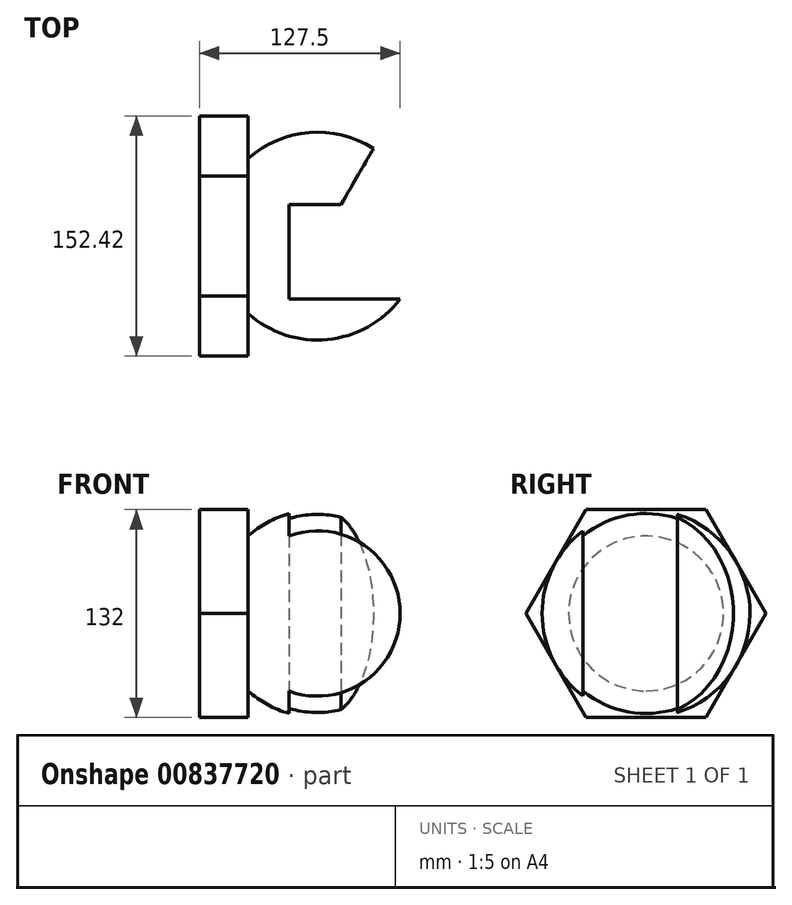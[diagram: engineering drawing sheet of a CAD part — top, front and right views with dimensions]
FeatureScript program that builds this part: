
annotation { "Feature Type Name" : "Feature", "Feature Type Description" : "" }
export const myFeature = defineFeature(function(context is Context, id is Id, definition is map)
    precondition{}
    {
        {
            var Q0;
            Q0=qCreatedBy(makeId("Right.planeOp"),FACE);
            var sketch = newSketch(context, id + "F0", { "sketchPlane" : qUnion([Q0])});
            skCircle(sketch, "E0.cCircle", {"center": v(0, 0) * mm, "radius": 66 * mm, "construction": true});
            skLineSegment(sketch, "E0.0", {"start": v(-38.1, 66) * mm, "end": v(38.1, 66) * mm});
            skLineSegment(sketch, "E0.1", {"start": v(38.1, 66) * mm, "end": v(76.21, 0) * mm});
            skLineSegment(sketch, "E0.2", {"start": v(76.21, 0) * mm, "end": v(38.1, -66) * mm});
            skLineSegment(sketch, "E0.3", {"start": v(38.1, -66) * mm, "end": v(-38.1, -66) * mm});
            skLineSegment(sketch, "E0.4", {"start": v(-38.1, -66) * mm, "end": v(-76.21, 0) * mm});
            skLineSegment(sketch, "E0.5", {"start": v(-76.21, 0) * mm, "end": v(-38.1, 66) * mm});
            skPoint(sketch, "E0.0.midPoint", {"position": v(0, 66) * mm});
            skSolve(sketch);
        }
        {
            var Q0;
            Q0=makeQuery(id+"F0.imprint","IMPRINT",FACE,{"disambiguationData":[TD([[makeQuery(id+"F0.imprint","IMPRINT",EDGE,{"derivedFrom":sQuery(id+"F0.wireOp",EDGE,"E0.0")}),-1.0]])]});
            extrude(context, id + "F1", {"entities" : qUnion([Q0]), "depth" : 31 * mm, "offsetDistance" : 25 * mm});
        }
        {
            var Q0;
            Q0=qCreatedBy(makeId("Front.planeOp"),FACE);
            var sketch = newSketch(context, id + "F2", { "sketchPlane" : qUnion([Q0])});
            skArc(sketch, "E1", {"start": v(141, 0) * mm, "mid": v(75, 66) * mm, "end": v(9, 0) * mm});
            skLineSegment(sketch, "E2.0.0", {"start": v(0, 66) * mm, "end": v(0, 0) * mm});
            skLineSegment(sketch, "E2.0.1", {"start": v(0, 0) * mm, "end": v(31, 0) * mm});
            skLineSegment(sketch, "E2.0.2", {"start": v(31, 0) * mm, "end": v(31, 66) * mm});
            skLineSegment(sketch, "E2.0.3", {"start": v(31, 66) * mm, "end": v(0, 66) * mm});
            skLineSegment(sketch, "E3.0.0", {"start": v(0, 0) * mm, "end": v(0, -66) * mm});
            skLineSegment(sketch, "E3.0.1", {"start": v(0, -66) * mm, "end": v(31, -66) * mm});
            skLineSegment(sketch, "E3.0.2", {"start": v(31, -66) * mm, "end": v(31, 0) * mm});
            skLineSegment(sketch, "E3.0.3", {"start": v(31, 0) * mm, "end": v(0, 0) * mm});
            skLineSegment(sketch, "E4", {"start": v(57, 66) * mm, "end": v(57, 63.5) * mm});
            skPoint(sketch, "E5.trimOffspring.end.orphan", {"position": v(57, -66) * mm});
            skLineSegment(sketch, "E6", {"start": v(141, 0) * mm, "end": v(9, 0) * mm});
            skSolve(sketch);
        }
        {
            var Q0;
            {var subQ0=sQuery(id+"F2.wireOp",EDGE,"E6");Q0=makeQuery(id+"F2.imprint","IMPRINT",FACE,{"disambiguationData":[TD([[makeQuery(id+"F2.imprint","IMPRINT",EDGE,{"derivedFrom":subQ0}),-1.0]])]});}
            var Q1;
            Q1=sQuery(id+"F2.wireOp",EDGE,"E6");
            revolve(context, id + "F3", {"operationType" : NewBodyOperationType.ADD, "surfaceOperationType" : NewSurfaceOperationType.NEW, "entities" : qUnion([Q0]), "axis" : qUnion([Q1]), "revolveType" : RevolveType.FULL});
        }
        {
            var Q0;
            Q0=makeQuery(id+"F1.opExtrude","SWEPT_FACE",FACE,{"disambiguationData":[OSD([sQuery(id+"F0.wireOp",EDGE,"E0.3")])]});
            cPlane(context, id + "F4", {"entities" : qUnion([Q0]), "cplaneType" : CPlaneType.OFFSET, "offset" : 0 * mm, "oppositeDirection" : true, "width" : 150 * mm, "height" : 150 * mm});
        }
        {
            var Q0;
            Q0=qCreatedBy(id+"F4.planeOp",FACE);
            var sketch = newSketch(context, id + "F5", { "sketchPlane" : qUnion([Q0])});
            skArc(sketch, "E7", {"start": v(31, -49.2) * mm, "mid": v(141, 0) * mm, "end": v(31, 49.2) * mm});
            skLineSegment(sketch, "E8", {"start": v(75, 40) * mm, "end": v(152.64, 40) * mm});
            skLineSegment(sketch, "E9", {"start": v(152.64, 40) * mm, "end": v(152.64, 0) * mm});
            skLineSegment(sketch, "E10", {"start": v(75, 40) * mm, "end": v(57, 40) * mm});
            skLineSegment(sketch, "E11", {"start": v(57, 40) * mm, "end": v(57, 0) * mm});
            skLineSegment(sketch, "E12", {"start": v(57, 0) * mm, "end": v(57, -20) * mm});
            skLineSegment(sketch, "E13", {"start": v(57, -20) * mm, "end": v(152.64, -20) * mm});
            skLineSegment(sketch, "E14", {"start": v(152.64, -20) * mm, "end": v(152.64, 0) * mm});
            skSolve(sketch);
        }
        {
            var Q0;
            {var subQ4=sQuery(id+"F5.wireOp",EDGE,"E10");Q0=makeQuery(id+"F5.imprint","IMPRINT",FACE,{"disambiguationData":[TD([[makeQuery(id+"F5.imprint","IMPRINT",EDGE,{"derivedFrom":subQ4}),1.0]])]});}
            extrude(context, id + "F6", {"entities" : qUnion([Q0]), "operationType" : NewBodyOperationType.REMOVE, "oppositeDirection" : true, "depth" : 138 * mm, "offsetDistance" : 25 * mm});
        }
        {
            var Q0;
            Q0=makeQuery(id+"F1.opExtrude","SWEPT_FACE",FACE,{"disambiguationData":[OSD([sQuery(id+"F0.wireOp",EDGE,"E0.3")])]});
            cPlane(context, id + "F7", {"entities" : qUnion([Q0]), "cplaneType" : CPlaneType.OFFSET, "offset" : 0 * mm, "width" : 150 * mm, "height" : 150 * mm});
        }
        {
            var Q0;
            Q0=qCreatedBy(id+"F7.planeOp",FACE);
            var sketch = newSketch(context, id + "F8", { "sketchPlane" : qUnion([Q0])});
            skArc(sketch, "E15", {"start": v(127.5, 40) * mm, "mid": v(9.97, -11.27) * mm, "end": v(137.9, -20) * mm});
            skLineSegment(sketch, "E16.0", {"start": v(57, 40) * mm, "end": v(127.5, 40) * mm});
            skLineSegment(sketch, "E17.0", {"start": v(57, 40) * mm, "end": v(57, -20) * mm});
            skLineSegment(sketch, "E18.0", {"start": v(57, -20) * mm, "end": v(137.9, -20) * mm});
            skLineSegment(sketch, "E19", {"start": v(75, -20) * mm, "end": v(90, -20) * mm});
            skLineSegment(sketch, "E20", {"start": v(90, -20) * mm, "end": v(110.56, -55.6) * mm});
            skSolve(sketch);
        }
        {
            var Q0;
            {var subQ3=sQuery(id+"F8.wireOp",EDGE,"E20");Q0=makeQuery(id+"F8.imprint","IMPRINT",FACE,{"disambiguationData":[TD([[makeQuery(id+"F8.imprint","IMPRINT",EDGE,{"derivedFrom":subQ3}),1.0]])]});}
            extrude(context, id + "F9", {"entities" : qUnion([Q0]), "operationType" : NewBodyOperationType.REMOVE, "oppositeDirection" : true, "depth" : 188 * mm, "offsetDistance" : 25 * mm});
        }
    });
